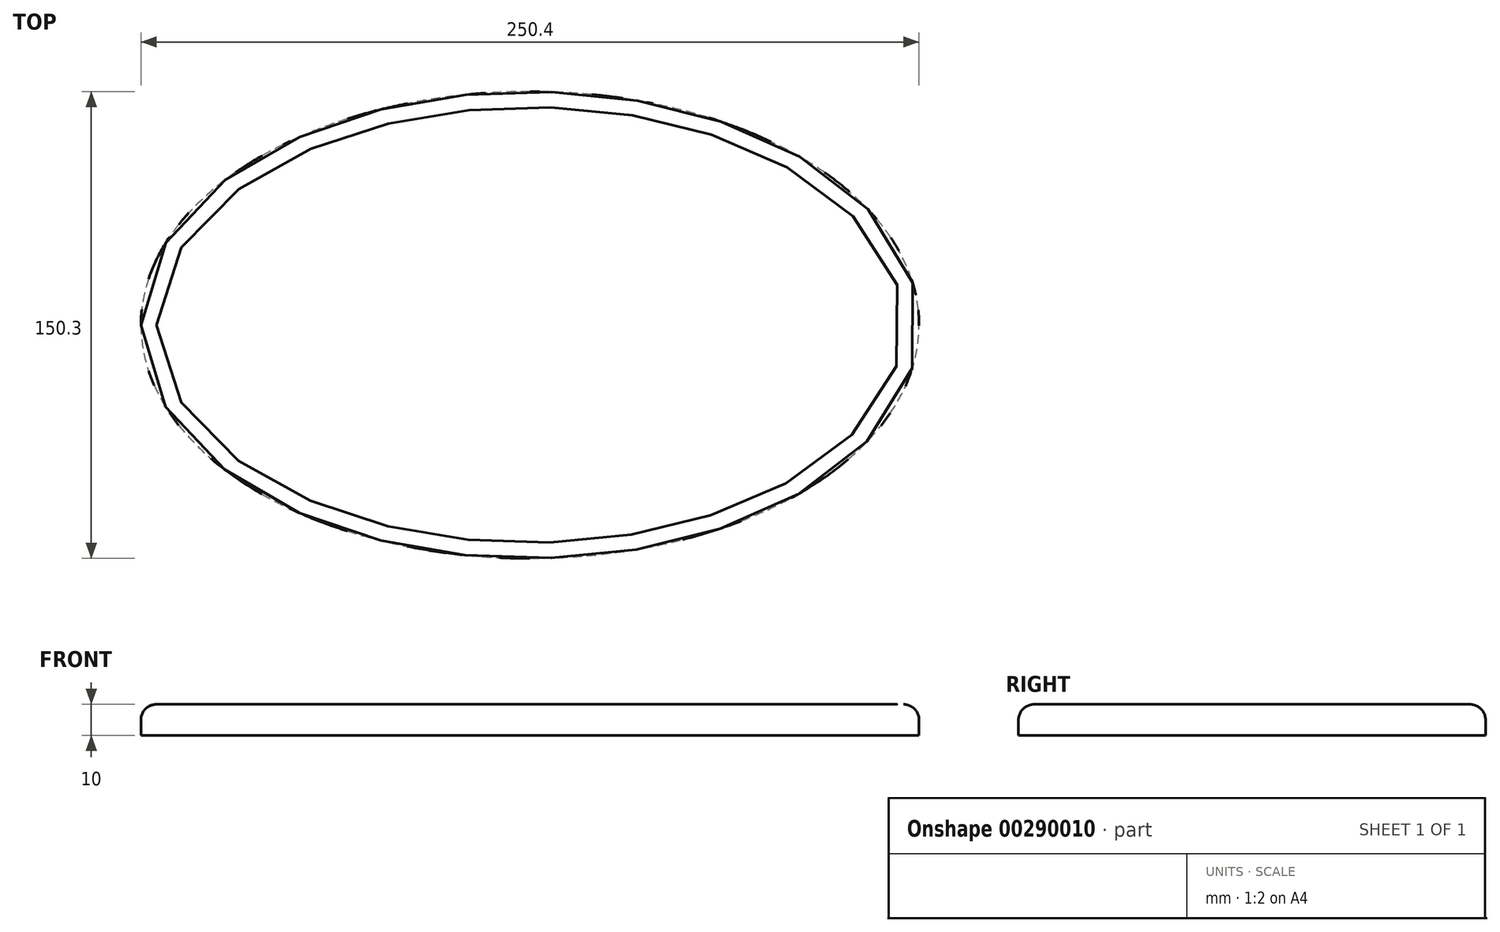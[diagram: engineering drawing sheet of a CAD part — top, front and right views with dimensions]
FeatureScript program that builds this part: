
annotation { "Feature Type Name" : "Feature", "Feature Type Description" : "" }
export const myFeature = defineFeature(function(context is Context, id is Id, definition is map)
    precondition{}
    {
        {
            var Q0;
            Q0=qCreatedBy(makeId("Top.planeOp"),FACE);
            var sketch = newSketch(context, id + "F0", { "sketchPlane" : qUnion([Q0])});
            skEllipse(sketch, "E0", {"center": v(0, 0) * mm, "majorRadius": 125.2 * mm, "minorRadius": 75.15 * mm, "majorAxis": v(-1, 0)});
            skSolve(sketch);
        }
        {
            var Q0;
            Q0=makeQuery(id+"F0.imprint","IMPRINT",FACE,{"disambiguationData":[TD([[makeQuery(id+"F0.imprint","IMPRINT",EDGE,{"derivedFrom":sQuery(id+"F0.wireOp",EDGE,"E0")}),1.0]])]});
            extrude(context, id + "F1", {"entities" : qUnion([Q0]), "depth" : 10 * mm});
        }
        {
            var Q0;
            Q0=makeQuery(id+"F1.opExtrude","CAP_EDGE",EDGE,{"disambiguationData":[OSD([sQuery(id+"F0.wireOp",EDGE,"E0")])],"isStart":false});
            fillet(context, id + "F2", {"entities" : qUnion([Q0]), "radius" : 5 * mm, "tangentPropagation" : true, "allowEdgeOverflow" : false});
        }
    });
